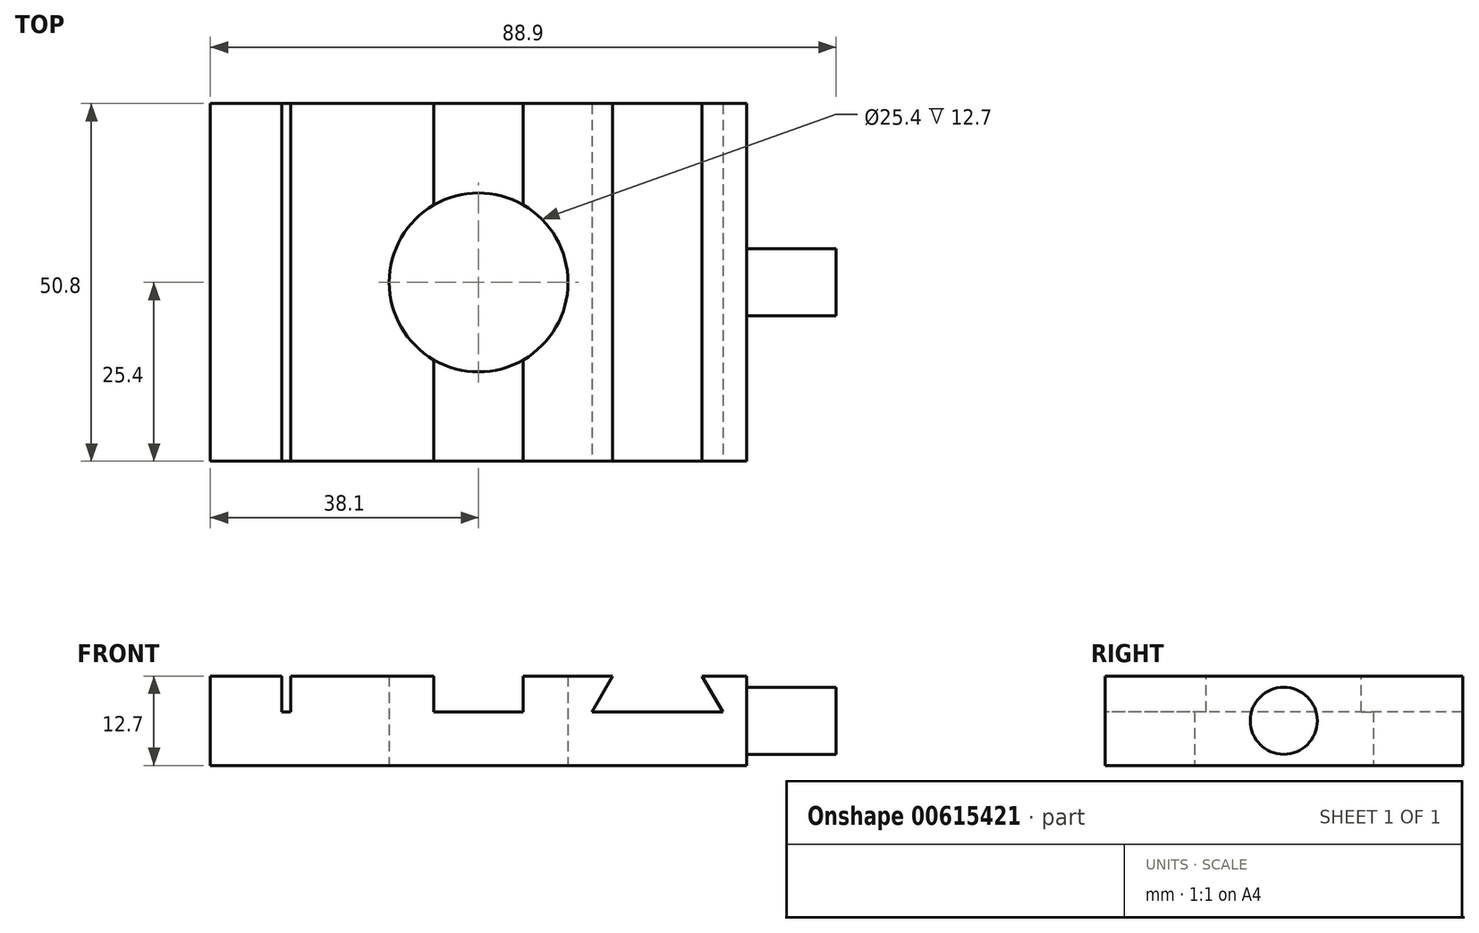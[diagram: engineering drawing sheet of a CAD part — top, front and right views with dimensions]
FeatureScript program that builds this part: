
annotation { "Feature Type Name" : "Feature", "Feature Type Description" : "" }
export const myFeature = defineFeature(function(context is Context, id is Id, definition is map)
    precondition{}
    {
        {
            var Q0;
            Q0=qCreatedBy(makeId("Top.planeOp"),FACE);
            var sketch = newSketch(context, id + "F0", { "sketchPlane" : qUnion([Q0])});
            skLineSegment(sketch, "E0.bottom", {"start": v(38.1, -25.4) * mm, "end": v(-38.1, -25.4) * mm});
            skLineSegment(sketch, "E0.top", {"start": v(38.1, 25.4) * mm, "end": v(-38.1, 25.4) * mm});
            skLineSegment(sketch, "E0.left", {"start": v(38.1, -25.4) * mm, "end": v(38.1, 25.4) * mm});
            skLineSegment(sketch, "E0.right", {"start": v(-38.1, -25.4) * mm, "end": v(-38.1, 25.4) * mm});
            skPoint(sketch, "E0.middle", {"position": v(0, 0) * mm});
            skCircle(sketch, "E1", {"center": v(0, 0) * mm, "radius": 12.7 * mm});
            skSolve(sketch);
        }
        {
            var Q0;
            Q0=makeQuery(id+"F0.imprint","IMPRINT",FACE,{"disambiguationData":[TD([[makeQuery(id+"F0.imprint","IMPRINT",EDGE,{"derivedFrom":sQuery(id+"F0.wireOp",EDGE,"E0.bottom")}),-1.0]])]});
            extrude(context, id + "F1", {"entities" : qUnion([Q0]), "depth" : 12.7 * mm, "offsetDistance" : 25.4 * mm});
        }
        {
            var Q0;
            Q0=makeQuery(id+"F1.opExtrude","CAP_FACE",FACE,{"disambiguationData":[OSD([sQuery(id+"F0.wireOp",EDGE,"E0.bottom"),sQuery(id+"F0.wireOp",EDGE,"E0.top"),sQuery(id+"F0.wireOp",EDGE,"E0.left"),sQuery(id+"F0.wireOp",EDGE,"E0.right"),sQuery(id+"F0.wireOp",EDGE,"E1")])],"isStart":false});
            var sketch = newSketch(context, id + "F2", { "sketchPlane" : qUnion([Q0])});
            skLineSegment(sketch, "E2.bottom", {"start": v(-27.94, 25.4) * mm, "end": v(-26.67, 25.4) * mm});
            skLineSegment(sketch, "E2.top", {"start": v(-27.94, -25.4) * mm, "end": v(-26.67, -25.4) * mm});
            skLineSegment(sketch, "E2.left", {"start": v(-27.94, 25.4) * mm, "end": v(-27.94, -25.4) * mm});
            skLineSegment(sketch, "E2.right", {"start": v(-26.67, 25.4) * mm, "end": v(-26.67, -25.4) * mm});
            skLineSegment(sketch, "E3", {"start": v(-6.35, 25.4) * mm, "end": v(-6.35, -25.4) * mm});
            skLineSegment(sketch, "E4", {"start": v(-6.35, -25.4) * mm, "end": v(6.35, -25.4) * mm});
            skLineSegment(sketch, "E5", {"start": v(6.35, -25.4) * mm, "end": v(6.35, 25.4) * mm});
            skLineSegment(sketch, "E6", {"start": v(0, 25.4) * mm, "end": v(0, -25.4) * mm, "construction": true});
            skLineSegment(sketch, "E7", {"start": v(-6.35, 25.4) * mm, "end": v(6.35, 25.4) * mm});
            skSolve(sketch);
        }
        {
            var Q0;
            Q0=makeQuery(id+"F2.imprint","IMPRINT",FACE,{"disambiguationData":[TD([[makeQuery(id+"F2.imprint","IMPRINT",EDGE,{"derivedFrom":sQuery(id+"F2.wireOp",EDGE,"E2.bottom")}),1.0]])]});
            var Q1;
            {var subQ0=sQuery(id+"F2.wireOp",EDGE,"E4");Q1=makeQuery(id+"F2.imprint","IMPRINT",FACE,{"disambiguationData":[TD([[makeQuery(id+"F2.imprint","IMPRINT",EDGE,{"derivedFrom":subQ0}),-1.0]])]});}
            var Q2;
            {var subQ0=sQuery(id+"F2.wireOp",EDGE,"E7");Q2=makeQuery(id+"F2.imprint","IMPRINT",FACE,{"disambiguationData":[TD([[makeQuery(id+"F2.imprint","IMPRINT",EDGE,{"derivedFrom":subQ0}),1.0]])]});}
            extrude(context, id + "F3", {"entities" : qUnion([Q0, Q1, Q2]), "operationType" : NewBodyOperationType.REMOVE, "oppositeDirection" : true, "depth" : 5.08 * mm, "offsetDistance" : 25.4 * mm});
        }
        {
            var Q0;
            Q0=makeQuery(id+"F1.opExtrude","SWEPT_FACE",FACE,{"disambiguationData":[OSD([sQuery(id+"F0.wireOp",EDGE,"E0.bottom")])]});
            var sketch = newSketch(context, id + "F4", { "sketchPlane" : qUnion([Q0])});
            skLineSegment(sketch, "E8", {"start": v(19.05, 12.7) * mm, "end": v(16.12, 7.62) * mm});
            skLineSegment(sketch, "E9", {"start": v(16.12, 7.62) * mm, "end": v(34.68, 7.62) * mm});
            skLineSegment(sketch, "E10", {"start": v(34.68, 7.62) * mm, "end": v(31.75, 12.7) * mm});
            skLineSegment(sketch, "E11", {"start": v(31.75, 12.7) * mm, "end": v(19.05, 12.7) * mm});
            skLineSegment(sketch, "E12", {"start": v(25.4, 7.62) * mm, "end": v(25.4, 12.7) * mm, "construction": true});
            skSolve(sketch);
        }
        {
            var Q0;
            Q0=makeQuery(id+"F4.imprint","IMPRINT",FACE,{"disambiguationData":[TD([[makeQuery(id+"F4.imprint","IMPRINT",EDGE,{"derivedFrom":sQuery(id+"F4.wireOp",EDGE,"E8")}),1.0]])]});
            extrude(context, id + "F5", {"entities" : qUnion([Q0]), "operationType" : NewBodyOperationType.REMOVE, "endBound" : BoundingType.THROUGH_ALL, "oppositeDirection" : true, "depth" : 25.4 * mm, "offsetDistance" : 25.4 * mm});
        }
        {
            var Q0;
            Q0=makeQuery(id+"F1.opExtrude","SWEPT_FACE",FACE,{"disambiguationData":[OSD([sQuery(id+"F0.wireOp",EDGE,"E0.left")])]});
            var sketch = newSketch(context, id + "F6", { "sketchPlane" : qUnion([Q0])});
            skCircle(sketch, "E13", {"center": v(0, 6.35) * mm, "radius": 4.76 * mm});
            skPoint(sketch, "E13.centerSnap0", {"position": v(-25.4, 6.35) * mm});
            skPoint(sketch, "E13.centerSnap1", {"position": v(0, 12.7) * mm});
            skSolve(sketch);
        }
        {
            var Q0;
            Q0=makeQuery(id+"F6.imprint","IMPRINT",FACE,{"disambiguationData":[TD([[makeQuery(id+"F6.imprint","IMPRINT",EDGE,{"derivedFrom":sQuery(id+"F6.wireOp",EDGE,"E13")}),1.0]])]});
            extrude(context, id + "F7", {"entities" : qUnion([Q0]), "operationType" : NewBodyOperationType.ADD, "depth" : 12.7 * mm, "offsetDistance" : 25.4 * mm});
        }
    });
